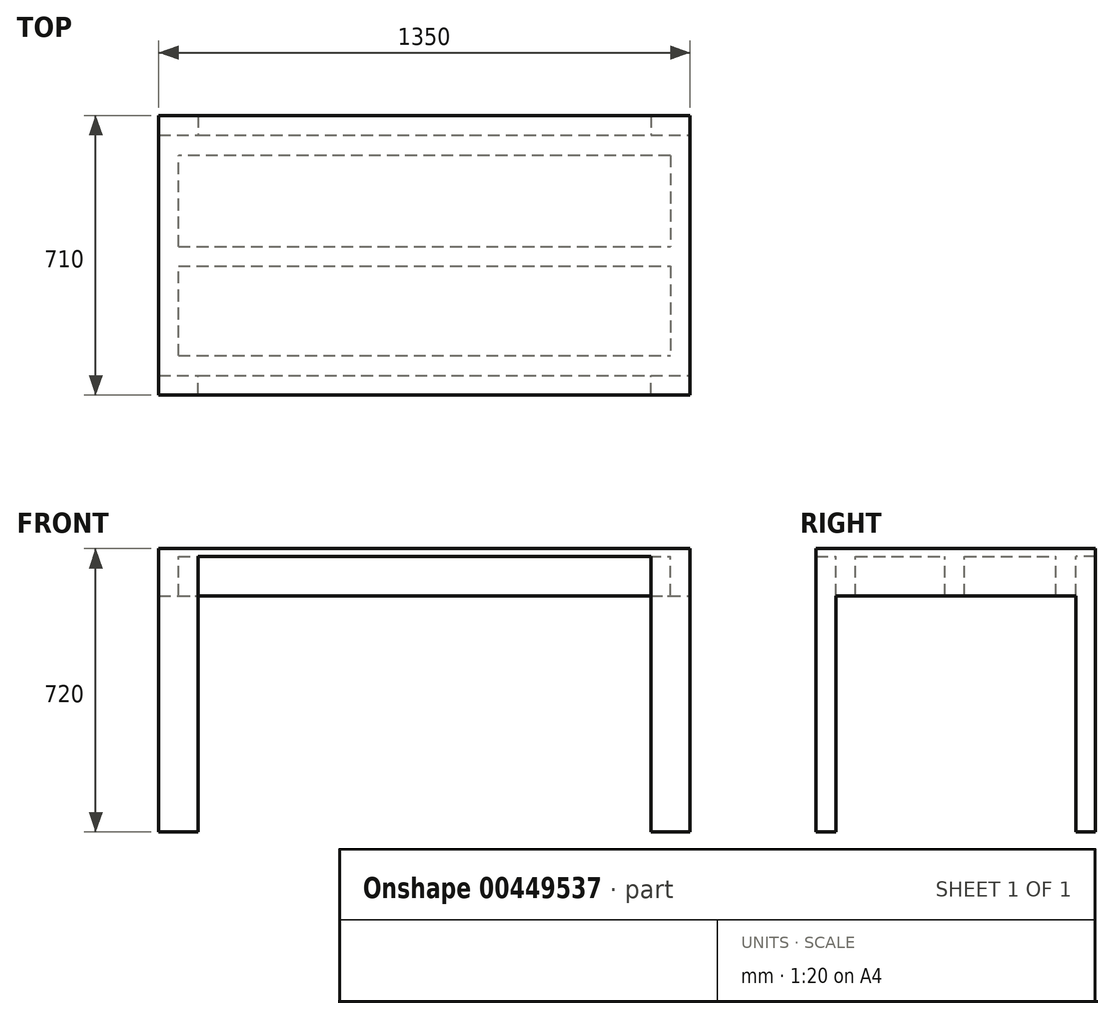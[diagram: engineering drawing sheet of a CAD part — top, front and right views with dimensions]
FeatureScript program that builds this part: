
annotation { "Feature Type Name" : "Feature", "Feature Type Description" : "" }
export const myFeature = defineFeature(function(context is Context, id is Id, definition is map)
    precondition{}
    {
        {
            var Q0;
            Q0=qCreatedBy(makeId("Top.planeOp"),FACE);
            var sketch = newSketch(context, id + "F0", { "sketchPlane" : qUnion([Q0])});
            skLineSegment(sketch, "E0.bottom", {"start": v(-675, 355) * mm, "end": v(675, 355) * mm});
            skLineSegment(sketch, "E0.top", {"start": v(-675, -355) * mm, "end": v(675, -355) * mm});
            skLineSegment(sketch, "E0.left", {"start": v(-675, 355) * mm, "end": v(-675, -355) * mm});
            skLineSegment(sketch, "E0.right", {"start": v(675, 355) * mm, "end": v(675, -355) * mm});
            skPoint(sketch, "E0.middle", {"position": v(0, 0) * mm});
            skSolve(sketch);
        }
        {
            var Q0;
            Q0=makeQuery(id+"F0.imprint","IMPRINT",FACE,{"disambiguationData":[TD([[makeQuery(id+"F0.imprint","IMPRINT",EDGE,{"derivedFrom":sQuery(id+"F0.wireOp",EDGE,"E0.bottom")}),-1.0]])]});
            extrude(context, id + "F1", {"entities" : qUnion([Q0]), "depth" : 20 * mm});
        }
        {
            var Q0;
            Q0=makeQuery(id+"F1.opExtrude","CAP_FACE",FACE,{"disambiguationData":[OSD([sQuery(id+"F0.wireOp",EDGE,"E0.bottom"),sQuery(id+"F0.wireOp",EDGE,"E0.top"),sQuery(id+"F0.wireOp",EDGE,"E0.left"),sQuery(id+"F0.wireOp",EDGE,"E0.right")])],"isStart":true});
            var sketch = newSketch(context, id + "F2", { "sketchPlane" : qUnion([Q0])});
            skLineSegment(sketch, "E1.bottom", {"start": v(-675, 355) * mm, "end": v(-575, 355) * mm});
            skLineSegment(sketch, "E1.top", {"start": v(-675, 305) * mm, "end": v(-575, 305) * mm});
            skLineSegment(sketch, "E1.left", {"start": v(-675, 355) * mm, "end": v(-675, 305) * mm});
            skLineSegment(sketch, "E1.right", {"start": v(-575, 355) * mm, "end": v(-575, 305) * mm});
            skLineSegment(sketch, "E2.bottom", {"start": v(675, 355) * mm, "end": v(575, 355) * mm});
            skLineSegment(sketch, "E2.top", {"start": v(675, 305) * mm, "end": v(575, 305) * mm});
            skLineSegment(sketch, "E2.left", {"start": v(675, 355) * mm, "end": v(675, 305) * mm});
            skLineSegment(sketch, "E2.right", {"start": v(575, 355) * mm, "end": v(575, 305) * mm});
            skLineSegment(sketch, "E3.bottom", {"start": v(675, -355) * mm, "end": v(575, -355) * mm});
            skLineSegment(sketch, "E3.top", {"start": v(675, -305) * mm, "end": v(575, -305) * mm});
            skLineSegment(sketch, "E3.left", {"start": v(675, -355) * mm, "end": v(675, -305) * mm});
            skLineSegment(sketch, "E3.right", {"start": v(575, -355) * mm, "end": v(575, -305) * mm});
            skLineSegment(sketch, "E4.bottom", {"start": v(-675, -355) * mm, "end": v(-575, -355) * mm});
            skLineSegment(sketch, "E4.top", {"start": v(-675, -305) * mm, "end": v(-575, -305) * mm});
            skLineSegment(sketch, "E4.left", {"start": v(-675, -355) * mm, "end": v(-675, -305) * mm});
            skLineSegment(sketch, "E4.right", {"start": v(-575, -355) * mm, "end": v(-575, -305) * mm});
            skSolve(sketch);
        }
        {
            var Q0;
            Q0=makeQuery(id+"F2.imprint","IMPRINT",FACE,{"disambiguationData":[TD([[makeQuery(id+"F2.imprint","IMPRINT",EDGE,{"derivedFrom":sQuery(id+"F2.wireOp",EDGE,"E3.bottom")}),1.0]])]});
            var Q1;
            Q1=makeQuery(id+"F2.imprint","IMPRINT",FACE,{"disambiguationData":[TD([[makeQuery(id+"F2.imprint","IMPRINT",EDGE,{"derivedFrom":sQuery(id+"F2.wireOp",EDGE,"E1.bottom")}),-1.0]])]});
            var Q2;
            Q2=makeQuery(id+"F2.imprint","IMPRINT",FACE,{"disambiguationData":[TD([[makeQuery(id+"F2.imprint","IMPRINT",EDGE,{"derivedFrom":sQuery(id+"F2.wireOp",EDGE,"E2.bottom")}),-1.0]])]});
            var Q3;
            Q3=makeQuery(id+"F2.imprint","IMPRINT",FACE,{"disambiguationData":[TD([[makeQuery(id+"F2.imprint","IMPRINT",EDGE,{"derivedFrom":sQuery(id+"F2.wireOp",EDGE,"E4.bottom")}),1.0]])]});
            extrude(context, id + "F3", {"entities" : qUnion([Q0, Q1, Q2, Q3]), "operationType" : NewBodyOperationType.ADD, "depth" : 700 * mm});
        }
        {
            var Q0;
            Q0=makeQuery(id+"F1.opExtrude","CAP_FACE",FACE,{"disambiguationData":[OSD([sQuery(id+"F0.wireOp",EDGE,"E0.bottom"),sQuery(id+"F0.wireOp",EDGE,"E0.top"),sQuery(id+"F0.wireOp",EDGE,"E0.left"),sQuery(id+"F0.wireOp",EDGE,"E0.right")])],"isStart":true});
            var sketch = newSketch(context, id + "F4", { "sketchPlane" : qUnion([Q0])});
            skLineSegment(sketch, "E5.bottom", {"start": v(-675, 305) * mm, "end": v(-625, 305) * mm});
            skLineSegment(sketch, "E5.top", {"start": v(-675, -305) * mm, "end": v(-625, -305) * mm});
            skLineSegment(sketch, "E5.left", {"start": v(-675, 305) * mm, "end": v(-675, -305) * mm});
            skLineSegment(sketch, "E5.right", {"start": v(-625, 305) * mm, "end": v(-625, -305) * mm});
            skLineSegment(sketch, "E6.bottom", {"start": v(675, -305) * mm, "end": v(625, -305) * mm});
            skLineSegment(sketch, "E6.top", {"start": v(675, 305) * mm, "end": v(625, 305) * mm});
            skLineSegment(sketch, "E6.left", {"start": v(675, -305) * mm, "end": v(675, 305) * mm});
            skLineSegment(sketch, "E6.right", {"start": v(625, -305) * mm, "end": v(625, 305) * mm});
            skLineSegment(sketch, "E7.bottom", {"start": v(-625, 305) * mm, "end": v(625, 305) * mm});
            skLineSegment(sketch, "E7.top", {"start": v(-625, 255) * mm, "end": v(625, 255) * mm});
            skLineSegment(sketch, "E7.left", {"start": v(-625, 305) * mm, "end": v(-625, 255) * mm});
            skLineSegment(sketch, "E7.right", {"start": v(625, 305) * mm, "end": v(625, 255) * mm});
            skLineSegment(sketch, "E8.bottom", {"start": v(625, -305) * mm, "end": v(-625, -305) * mm});
            skLineSegment(sketch, "E8.top", {"start": v(625, -253.85) * mm, "end": v(-625, -253.85) * mm});
            skLineSegment(sketch, "E8.left", {"start": v(625, -305) * mm, "end": v(625, -253.85) * mm});
            skLineSegment(sketch, "E8.right", {"start": v(-625, -305) * mm, "end": v(-625, -253.85) * mm});
            skLineSegment(sketch, "E9.bottom", {"start": v(-625, 27.9) * mm, "end": v(625, 27.9) * mm});
            skLineSegment(sketch, "E9.top", {"start": v(-625, -22.1) * mm, "end": v(625, -22.1) * mm});
            skLineSegment(sketch, "E9.left", {"start": v(-625, 27.9) * mm, "end": v(-625, -22.1) * mm});
            skLineSegment(sketch, "E9.right", {"start": v(625, 27.9) * mm, "end": v(625, -22.1) * mm});
            skSolve(sketch);
        }
        {
            var Q0;
            Q0=makeQuery(id+"F4.imprint","IMPRINT",FACE,{"disambiguationData":[TD([[makeQuery(id+"F4.imprint","IMPRINT",EDGE,{"derivedFrom":sQuery(id+"F4.wireOp",EDGE,"E5.bottom")}),-1.0]])]});
            var Q1;
            Q1=makeQuery(id+"F4.imprint","IMPRINT",FACE,{"disambiguationData":[TD([[makeQuery(id+"F4.imprint","IMPRINT",EDGE,{"derivedFrom":sQuery(id+"F4.wireOp",EDGE,"E7.top")}),1.0]])]});
            var Q2;
            Q2=makeQuery(id+"F4.imprint","IMPRINT",FACE,{"disambiguationData":[TD([[makeQuery(id+"F4.imprint","IMPRINT",EDGE,{"derivedFrom":sQuery(id+"F4.wireOp",EDGE,"E8.top")}),1.0]])]});
            var Q3;
            Q3=makeQuery(id+"F4.imprint","IMPRINT",FACE,{"disambiguationData":[TD([[makeQuery(id+"F4.imprint","IMPRINT",EDGE,{"derivedFrom":sQuery(id+"F4.wireOp",EDGE,"E6.bottom")}),-1.0]])]});
            var Q4;
            Q4=makeQuery(id+"F4.imprint","IMPRINT",FACE,{"disambiguationData":[TD([[makeQuery(id+"F4.imprint","IMPRINT",EDGE,{"derivedFrom":sQuery(id+"F4.wireOp",EDGE,"E9.bottom")}),-1.0]])]});
            extrude(context, id + "F5", {"entities" : qUnion([Q0, Q1, Q2, Q3, Q4]), "operationType" : NewBodyOperationType.ADD, "depth" : 100 * mm});
        }
    });
